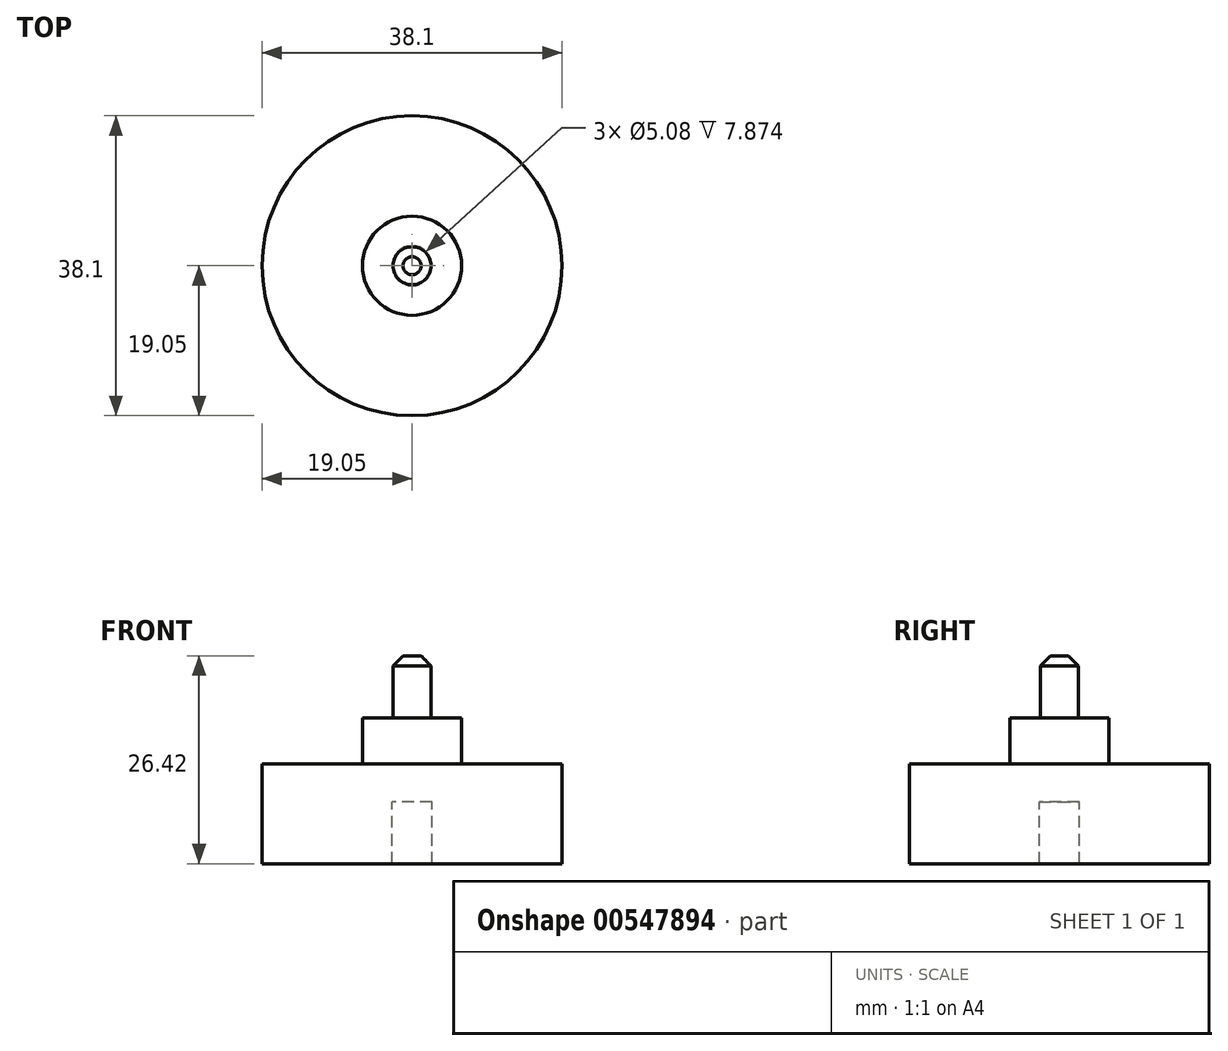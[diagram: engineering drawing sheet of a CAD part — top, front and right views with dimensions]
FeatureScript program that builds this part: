
annotation { "Feature Type Name" : "Feature", "Feature Type Description" : "" }
export const myFeature = defineFeature(function(context is Context, id is Id, definition is map)
    precondition{}
    {
        {
            var Q0;
            Q0=qCreatedBy(makeId("Front.planeOp"),FACE);
            var sketch = newSketch(context, id + "F0", { "sketchPlane" : qUnion([Q0])});
            skLineSegment(sketch, "E0", {"start": v(2.54, 0) * mm, "end": v(19.05, 0) * mm});
            skLineSegment(sketch, "E1", {"start": v(19.05, 0) * mm, "end": v(19.05, 12.7) * mm});
            skLineSegment(sketch, "E2", {"start": v(19.05, 12.7) * mm, "end": v(6.3, 12.7) * mm});
            skLineSegment(sketch, "E3", {"start": v(6.3, 18.54) * mm, "end": v(6.3, 12.7) * mm});
            skPoint(sketch, "E4.orphan", {"position": v(6.3, 0) * mm});
            skPoint(sketch, "E5.start.orphan", {"position": v(0, 12.7) * mm});
            skLineSegment(sketch, "E6", {"start": v(2.54, 0) * mm, "end": v(2.54, 7.87) * mm});
            skLineSegment(sketch, "E7", {"start": v(2.54, 7.87) * mm, "end": v(0, 7.87) * mm});
            skPoint(sketch, "E8.orphan", {"position": v(0, 0) * mm});
            skLineSegment(sketch, "E9", {"start": v(0, 26.42) * mm, "end": v(0, 7.87) * mm});
            skLineSegment(sketch, "E10", {"start": v(0, 26.42) * mm, "end": v(2.41, 26.42) * mm});
            skLineSegment(sketch, "E11", {"start": v(2.41, 26.42) * mm, "end": v(2.41, 18.54) * mm});
            skLineSegment(sketch, "E12", {"start": v(6.3, 18.54) * mm, "end": v(2.41, 18.54) * mm});
            skSolve(sketch);
        }
        {
            var Q0;
            Q0 = qSketchRegion(id + "F0", true);
            var Q1;
            Q1=sQuery(id+"F0.wireOp",EDGE,"E9");
            revolve(context, id + "F1", {"entities" : qUnion([Q0]), "axis" : qUnion([Q1]), "revolveType" : RevolveType.FULL});
        }
        {
            var Q0;
            Q0=makeQuery(id+"F1.opRevolve","SWEPT_EDGE",EDGE,{"disambiguationData":[OSD([sQuery(id+"F0.wireOp",EDGE,"E10"),sQuery(id+"F0.wireOp",EDGE,"E11")])]});
            chamfer(context, id + "F2", {"entities" : qUnion([Q0]), "width" : 1.27 * mm, "tangentPropagation" : true});
        }
    });
